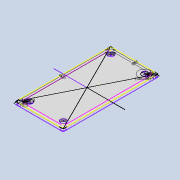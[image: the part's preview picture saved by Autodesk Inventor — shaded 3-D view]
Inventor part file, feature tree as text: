
AUTODESK INVENTOR PART (.ipt)
format: ipt  version: 2020 (Build 240168000, 168)  size: 189,952 bytes
history: native  units: mm
features: sketch x3, extrude x2, fillet x1
ambient origin geometry x8: Origin, YZ Plane, XZ Plane, XY Plane, X Axis, Y Axis, Z Axis, Center Point
bodies: Body1 (feature_tree)
feature tree (6):
  sketch  "Sketch1"  dims[d0=45.0mm d1=90.0mm d2=40.0mm]
  extrude  "Extrusion3"  Depth=90.0mm
  fillet  "Fillet1"  Radius=40.0mm
  sketch  "Sketch2"  dims[d3=85.0mm d8=2.5mm]
  extrude  "Extrusion10"  Depth=2.5mm
  sketch  "Sketch4"  dims[d9=2.5mm d24=2.5mm d25=0.0mm d28=3.0mm d29=1.5mm d30=1.5mm d31=2.75mm d32=5.5mm d33=1.5mm d34=1.5mm d35=2.75mm d36=45.0deg d37=5.5mm d38=20.0mm d40=360.0deg d43=20.0mm d44=1.2mm d45=1.2mm d60=10.0mm d61=0.0mm d58=0.5mm d59=0.872665mm]
